# Revit family: Mechanical_Equipment-GE-Zoneline_VTAC-UltimateV10-AirConditioner-Vertical-AZ95
name_source: partatom
category: Mechanical Equipment
revit_build: Autodesk Revit 2018 (Build: 20190510_1515(x64)
units: mm (PartAtom-declared; Revit-internal decimal feet)

## family parameters
Always vertical = Yes
Cut with Voids When Loaded = No
OmniClass Number = 23.75.70.21.21
OmniClass Title = Local Air-Conditioning Units
Part Type = Normal
Room Calculation Point = No
Round Connector Dimension = Use Diameter
Shared = No
Work Plane-Based = No

## types (17) — shared parameters
Air Supply Diamter = 10"
Apparent Load = 0 VA
Assembly Code = D3040
Depth = 2' - 0 1/8"
Description = Vertical Air Conditioner
Frequency = 60 Hz
Height = 2' - 7 7/8"
Housing Material = Metal - GE - Sheet Metal
Keynote = 23 30 00
Manufacturer = GE Appliances
Number of Poles = 1
Phase = 1
Power Factor = 1
Product Name = GE Zoneline® Heat Pump Single Package Vertical Air Conditioner (VTAC) - UltimateV10
Product Page URL = https://products.geappliances.com
Return Air Height = 1' - 2"
Return Air Width = 1' - 8"
URL = https://www.geappliances.com
Version = 2018 v.1.0a
Voltage = 230 V
Warranty URL = https://www.geappliances.com
Width = 1' - 11 5/8"

## type names (no varying parameters)
- AZ90E09D2C
- AZ90E09D3C
- AZ90E09D5C
- AZ90E12D2C
- AZ90E12D3C
- AZ90E12D5C
- AZ90E18D2C
- AZ90E18D3C
- AZ91H09D2E
- AZ91H09D5E
- AZ91H09E2E
- AZ91H09E3E
- AZ91H09E5E
- AZ91H12D2E
- AZ91H12D5E
- AZ91H12E3E
- AZ91H12E5E

note: column(s) folded — value = type name in every type: Model

## geometry (parser evidence)
native form markers: Sweep x2
no freeform markers — native parametric forms only
